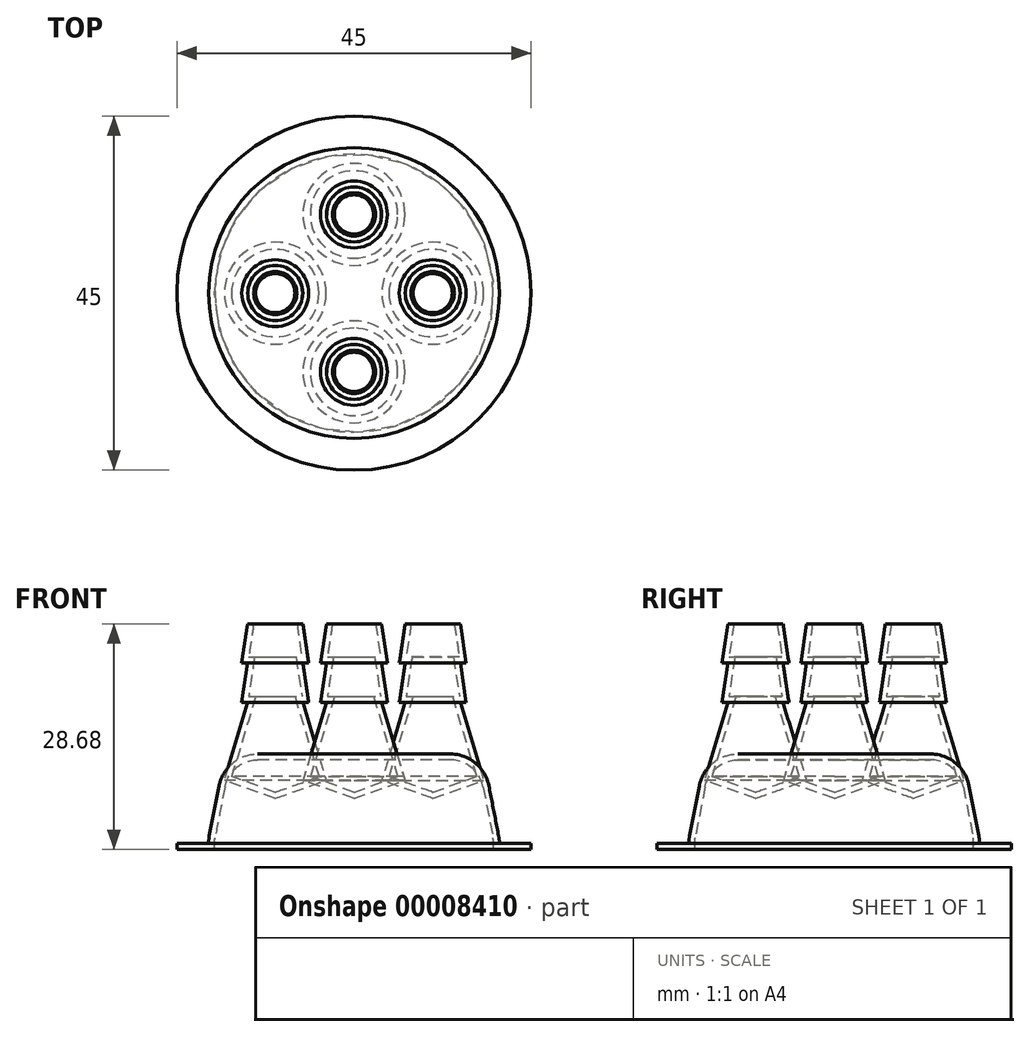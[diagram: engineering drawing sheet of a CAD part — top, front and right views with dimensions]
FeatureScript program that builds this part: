
annotation { "Feature Type Name" : "Feature", "Feature Type Description" : "" }
export const myFeature = defineFeature(function(context is Context, id is Id, definition is map)
    precondition{}
    {
        {
            var Q0;
            Q0=qCreatedBy(makeId("Right.planeOp"),FACE);
            var sketch = newSketch(context, id + "F0", { "sketchPlane" : qUnion([Q0])});
            skLineSegment(sketch, "E0", {"start": v(-22.5, 0) * mm, "end": v(0, 0) * mm});
            skLineSegment(sketch, "E1", {"start": v(-22.5, 0) * mm, "end": v(-22.5, 0.75) * mm});
            skLineSegment(sketch, "E2", {"start": v(-22.5, 0.75) * mm, "end": v(-18.47, 0.75) * mm});
            skLineSegment(sketch, "E3", {"start": v(-18.47, 0.75) * mm, "end": v(-18.47, 0.75) * mm});
            skLineSegment(sketch, "E4", {"start": v(-17.13, 8.1) * mm, "end": v(-18.38, 1.7) * mm});
            skArc(sketch, "E5.filletArc", {"start": v(-18.38, 1.7) * mm, "mid": v(-18.45, 1.23) * mm, "end": v(-18.47, 0.75) * mm});
            skLineSegment(sketch, "E6", {"start": v(-17.13, 4.16) * mm, "end": v(-17.87, 4.3) * mm, "construction": true});
            skLineSegment(sketch, "E7", {"start": v(0, 12.14) * mm, "end": v(-12.23, 12.14) * mm});
            skPoint(sketch, "E8.visualSharp", {"position": v(-13.28, 25.08) * mm});
            skPoint(sketch, "E9.visualSharp", {"position": v(-16.35, 12.14) * mm});
            skArc(sketch, "E9.filletArc", {"start": v(-12.23, 12.14) * mm, "mid": v(-15.4, 11) * mm, "end": v(-17.13, 8.1) * mm});
            skLineSegment(sketch, "E10", {"start": v(0, 28.05) * mm, "end": v(0, 0) * mm, "construction": true});
            skLineSegment(sketch, "E11", {"start": v(0, 12.14) * mm, "end": v(0, 0) * mm});
            skSolve(sketch);
        }
        {
            var Q0;
            Q0 = qSketchRegion(id + "F0", true);
            var Q1;
            Q1=sQuery(id+"F0.wireOp",EDGE,"E10");
            revolve(context, id + "F1", {"entities" : qUnion([Q0]), "axis" : qUnion([Q1]), "revolveType" : RevolveType.FULL});
        }
        {
            var Q0;
            Q0=qCreatedBy(makeId("Front.planeOp"),FACE);
            var sketch = newSketch(context, id + "F2", { "sketchPlane" : qUnion([Q0])});
            skLineSegment(sketch, "E12", {"start": v(-10, 28.68) * mm, "end": v(-13.5, 28.68) * mm});
            skLineSegment(sketch, "E13", {"start": v(-13.5, 28.68) * mm, "end": v(-14.25, 23.68) * mm});
            skLineSegment(sketch, "E14", {"start": v(-14.25, 23.68) * mm, "end": v(-13.5, 23.68) * mm});
            skLineSegment(sketch, "E15", {"start": v(-13.5, 23.68) * mm, "end": v(-14.25, 18.68) * mm});
            skLineSegment(sketch, "E16", {"start": v(-14.25, 18.68) * mm, "end": v(-13.5, 18.68) * mm});
            skLineSegment(sketch, "E17", {"start": v(-13.5, 18.68) * mm, "end": v(-16.47, 8.8) * mm});
            skLineSegment(sketch, "E18", {"start": v(-13.5, 28.68) * mm, "end": v(-13.5, 23.68) * mm, "construction": true});
            skLineSegment(sketch, "E19", {"start": v(-13.5, 18.68) * mm, "end": v(-13.5, 23.68) * mm, "construction": true});
            skLineSegment(sketch, "E20", {"start": v(-10, 28.68) * mm, "end": v(-10, 6.49) * mm});
            skLineSegment(sketch, "E21", {"start": v(-16.47, 8.8) * mm, "end": v(-10, 6.49) * mm});
            skSolve(sketch);
        }
        {
            var Q0;
            Q0 = qSketchRegion(id + "F2", true);
            var Q1;
            Q1=sQuery(id+"F2.wireOp",EDGE,"E20");
            revolve(context, id + "F3", {"entities" : qUnion([Q0]), "axis" : qUnion([Q1]), "revolveType" : RevolveType.FULL});
        }
        {
            var Q0;
            Q0=makeQuery(id+"F3.opRevolve","SWEPT_BODY",BODY,{"disambiguationData":[OSD([sQuery(id+"F2.wireOp",EDGE,"E12"),sQuery(id+"F2.wireOp",EDGE,"E13"),sQuery(id+"F2.wireOp",EDGE,"E14"),sQuery(id+"F2.wireOp",EDGE,"E15"),sQuery(id+"F2.wireOp",EDGE,"E16"),sQuery(id+"F2.wireOp",EDGE,"E17"),sQuery(id+"F2.wireOp",EDGE,"E20"),sQuery(id+"F2.wireOp",EDGE,"E21")])]});
            var Q1;
            Q1=sQuery(id+"F0.wireOp",EDGE,"E10");
            circularPattern(context, id + "F4", {"entities" : qUnion([Q0]), "axis" : qUnion([Q1]), "angle" : 90 * degree, "instanceCount" : 4});
        }
        {
            var Q0;
            Q0=makeQuery(id+"F3.opRevolve","SWEPT_FACE",FACE,{"disambiguationData":[OSD([sQuery(id+"F2.wireOp",EDGE,"E12")])]});
            var Q1;
            Q1=makeQuery(id+"F4.opPattern","COPY",FACE,{"derivedFrom":makeQuery(id+"F3.opRevolve","SWEPT_FACE",FACE,{"disambiguationData":[OSD([sQuery(id+"F2.wireOp",EDGE,"E12")])]}),"instanceName":"1"});
            var Q2;
            Q2=makeQuery(id+"F4.opPattern","COPY",FACE,{"derivedFrom":makeQuery(id+"F3.opRevolve","SWEPT_FACE",FACE,{"disambiguationData":[OSD([sQuery(id+"F2.wireOp",EDGE,"E12")])]}),"instanceName":"2"});
            var Q3;
            Q3=makeQuery(id+"F4.opPattern","COPY",FACE,{"derivedFrom":makeQuery(id+"F3.opRevolve","SWEPT_FACE",FACE,{"disambiguationData":[OSD([sQuery(id+"F2.wireOp",EDGE,"E12")])]}),"instanceName":"3"});
            var Q4;
            Q4=makeQuery(id+"F1.opRevolve","SWEPT_FACE",FACE,{"disambiguationData":[OSD([sQuery(id+"F0.wireOp",EDGE,"E0")])]});
            shell(context, id + "F5", {"entities" : qUnion([Q0, Q1, Q2, Q3, Q4]), "thickness" : 0.75 * mm});
        }
    });
